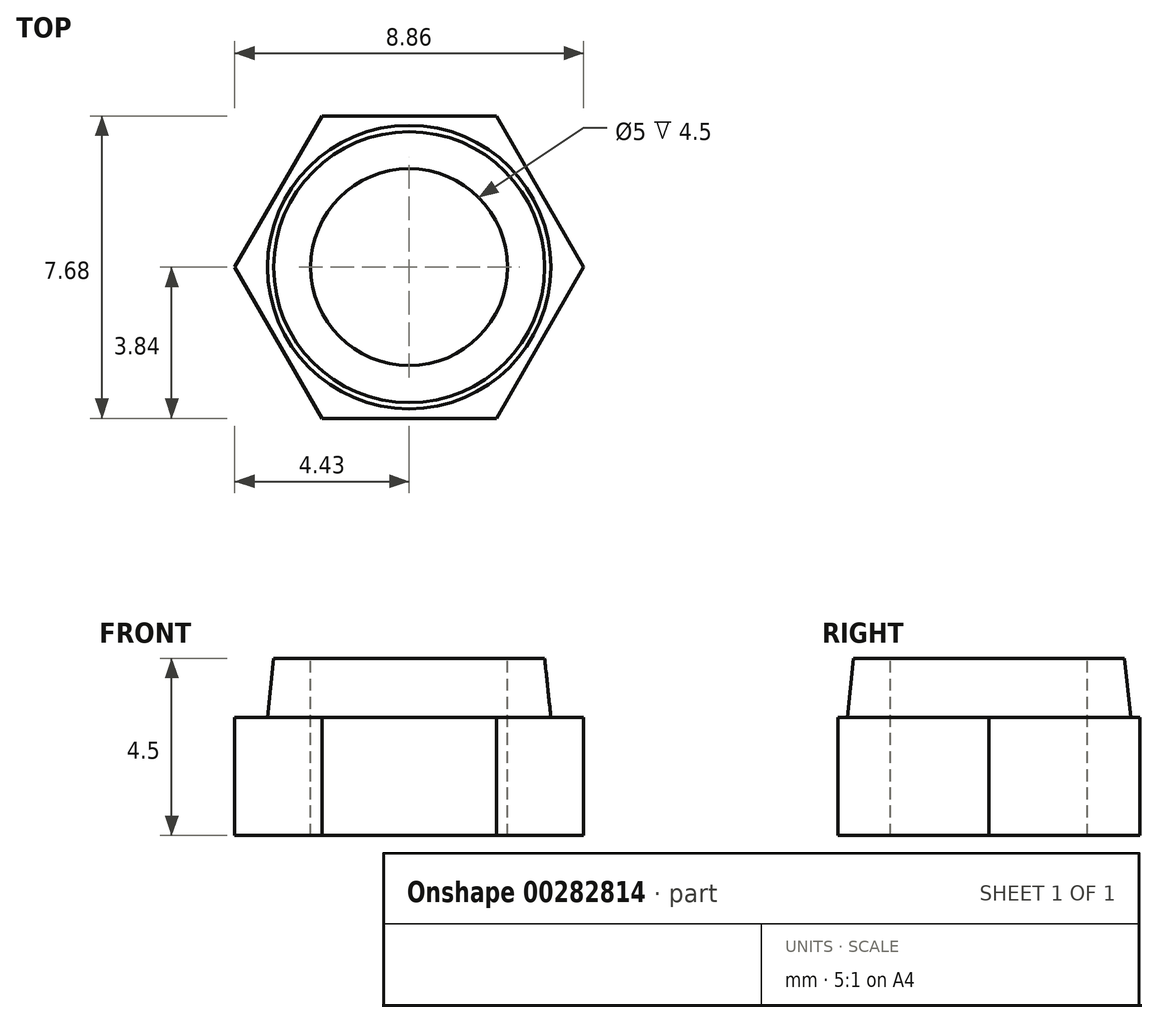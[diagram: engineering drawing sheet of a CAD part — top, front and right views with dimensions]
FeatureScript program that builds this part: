
annotation { "Feature Type Name" : "Feature", "Feature Type Description" : "" }
export const myFeature = defineFeature(function(context is Context, id is Id, definition is map)
    precondition{}
    {
        {
            var Q0;
            Q0=qCreatedBy(makeId("Top.planeOp"),FACE);
            var sketch = newSketch(context, id + "F0", { "sketchPlane" : qUnion([Q0])});
            skCircle(sketch, "E0.cCircle", {"center": v(0, 0) * mm, "radius": 3.84 * mm, "construction": true});
            skLineSegment(sketch, "E0.0", {"start": v(-2.22, 3.84) * mm, "end": v(2.22, 3.84) * mm});
            skLineSegment(sketch, "E0.1", {"start": v(2.22, 3.84) * mm, "end": v(4.43, 0) * mm});
            skLineSegment(sketch, "E0.2", {"start": v(4.43, 0) * mm, "end": v(2.22, -3.84) * mm});
            skLineSegment(sketch, "E0.3", {"start": v(2.22, -3.84) * mm, "end": v(-2.22, -3.84) * mm});
            skLineSegment(sketch, "E0.4", {"start": v(-2.22, -3.84) * mm, "end": v(-4.43, 0) * mm});
            skLineSegment(sketch, "E0.5", {"start": v(-4.43, 0) * mm, "end": v(-2.22, 3.84) * mm});
            skPoint(sketch, "E0.0.midPoint", {"position": v(0, 3.84) * mm});
            skSolve(sketch);
        }
        {
            var Q0;
            Q0=qSketchRegion(id+"F0",true);
            extrude(context, id + "F1", {"entities" : qUnion([Q0]), "depth" : 3 * mm});
        }
        {
            var Q0;
            Q0=makeQuery(id+"F1.opExtrude","CAP_FACE",FACE,{"disambiguationData":[OSD([sQuery(id+"F0.wireOp",EDGE,"E0.0"),sQuery(id+"F0.wireOp",EDGE,"E0.1"),sQuery(id+"F0.wireOp",EDGE,"E0.2"),sQuery(id+"F0.wireOp",EDGE,"E0.3"),sQuery(id+"F0.wireOp",EDGE,"E0.4"),sQuery(id+"F0.wireOp",EDGE,"E0.5")])],"isStart":false});
            var sketch = newSketch(context, id + "F2", { "sketchPlane" : qUnion([Q0])});
            skCircle(sketch, "E1", {"center": v(0, 0) * mm, "radius": 3.6 * mm});
            skSolve(sketch);
        }
        {
            var Q0;
            Q0=qSketchRegion(id+"F2",true);
            extrude(context, id + "F3", {"entities" : qUnion([Q0]), "operationType" : NewBodyOperationType.ADD, "depth" : 1.5 * mm, "hasDraft" : true, "draftAngle" : 6 * degree, "draftPullDirection" : true});
        }
        {
            var Q0;
            Q0=makeQuery(id+"F3.opExtrude","CAP_FACE",FACE,{"disambiguationData":[OSD([sQuery(id+"F2.wireOp",EDGE,"E1")])],"isStart":false});
            var sketch = newSketch(context, id + "F4", { "sketchPlane" : qUnion([Q0])});
            skCircle(sketch, "E2", {"center": v(0, 0) * mm, "radius": 2.5 * mm});
            skSolve(sketch);
        }
        {
            var Q0;
            Q0=qSketchRegion(id+"F4",true);
            extrude(context, id + "F5", {"entities" : qUnion([Q0]), "operationType" : NewBodyOperationType.REMOVE, "endBound" : BoundingType.THROUGH_ALL, "oppositeDirection" : true, "depth" : 25 * mm});
        }
    });
